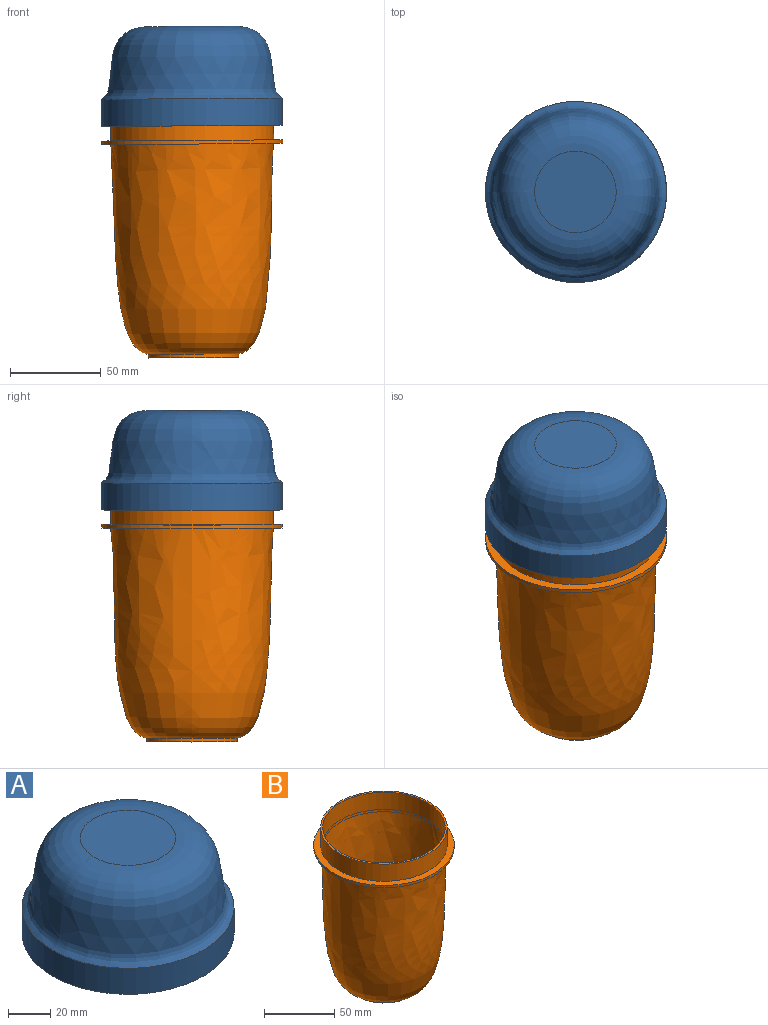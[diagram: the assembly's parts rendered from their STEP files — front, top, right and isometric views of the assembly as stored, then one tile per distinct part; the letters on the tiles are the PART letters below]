
ASSEMBLY  parts=2 mates=1
PART A: 7 faces, bbox 100x100x55 mm
  f0: plane 45x45mm, normal (0,0,-1), area 1590.4mm2, adj f1
  f1: revolved ~96x96mm, area 12872.4mm2, adj f0,f2
  f2: cylinder r=48mm len=96mm, axis (0,0,-1), area 4220.9mm2, adj f1,f3
  f3: plane 100x100mm, normal (0,0,-1), area 615.8mm2, adj f2,f4
  f4: cylinder r=50mm len=100mm, axis (0,0,-1), area 4712.4mm2, adj f3,f5
  f5: revolved ~100x100mm, area 13857.3mm2, adj f4,f6
  f6: plane 45x45mm, normal (0,0,1), area 1590.4mm2, adj f5
PART B: 14 faces, bbox 100x100x135 mm
  f0: revolved ~116x89.84mm, area 31411.5mm2, adj f1,f13
  f1: plane 100x100mm, normal (0,0,-1), area 1514.4mm2, adj f0,f2
  f2: cylinder r=50mm len=100mm, axis (0,0,-1), area 628.3mm2, adj f1,f3
  f3: plane 100x100mm, normal (0,0,1), area 1492.3mm2, adj f2,f4
  f4: cylinder r=45mm len=90mm, axis (0,0,-1), area 4241.2mm2, adj f3,f5
  f5: plane 90x90mm, normal (0,0,1), area 417mm2, adj f4,f6
  f6: cylinder r=43.5mm len=87mm, axis (0,0,-1), area 4091.7mm2, adj f5,f7
  f7: cone r=43.5mm half-angle=2.2deg, axis (0,0,1), area 529.3mm2, adj f6,f8
  f8: revolved ~113.09x86.85mm, area 58395.4mm2, adj f7,f9
  f9: plane 57.44x57.44mm, normal (0,0,1), area 2591.2mm2, adj f8
  f10: plane 48x48mm, normal (0,0,-1), area 1809.6mm2, adj f11
  f11: cylinder r=24mm len=48mm, axis (0,0,-1), area 301.6mm2, adj f10,f12
  f12: plane 50x50mm, normal (0,0,-1), area 153.9mm2, adj f11,f13
  f13: cylinder r=25mm len=50mm, axis (0,0,-1), area 314.2mm2, adj f0,f12
PLACE A rot(axis=(0,-1,0),0.4deg) t=(-33.04,-1.26,95.92)mm
PLACE B rot(axis=(0,-1,0),0.4deg) t=(-33.24,-1.26,125.45)mm
MATE cylindrical A.f2 <-> B.f2  axis (0.01,0,-1) through (-34.16,-1.26,260.48)mm
